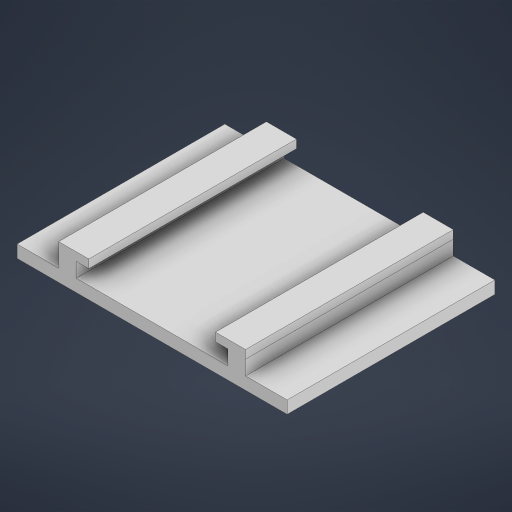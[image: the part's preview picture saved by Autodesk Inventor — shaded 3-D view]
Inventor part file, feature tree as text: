
AUTODESK INVENTOR PART (.ipt)
format: ipt  version: 2023 (Build 270158000, 158)  size: 220,672 bytes
history: native  units: mm
features: extrude x3, sketch x3
ambient origin geometry x8: Origin, YZ Plane, XZ Plane, XY Plane, X Axis, Y Axis, Z Axis, Center Point
bodies: Solid1 (feature_tree)
feature tree (6):
  extrude  "Extrusion1"  Depth=50.0mm
  extrude  "Extrusion2"  Depth=36.5mm
  extrude  "Extrusion3"  Depth=3.5mm TaperAngle=0.0deg
  sketch  "Sketch1"  dims[d0=65.0mm d1=50.0mm]
  sketch  "Sketch2"  dims[d2=3.0mm d3=0.0mm d4=36.5mm]
  sketch  "Sketch3"  dims[d5=45.0mm d6=3.5mm d7=0.0mm d8=7.25mm d9=7.25mm d10=2.0mm d11=0.0mm]
